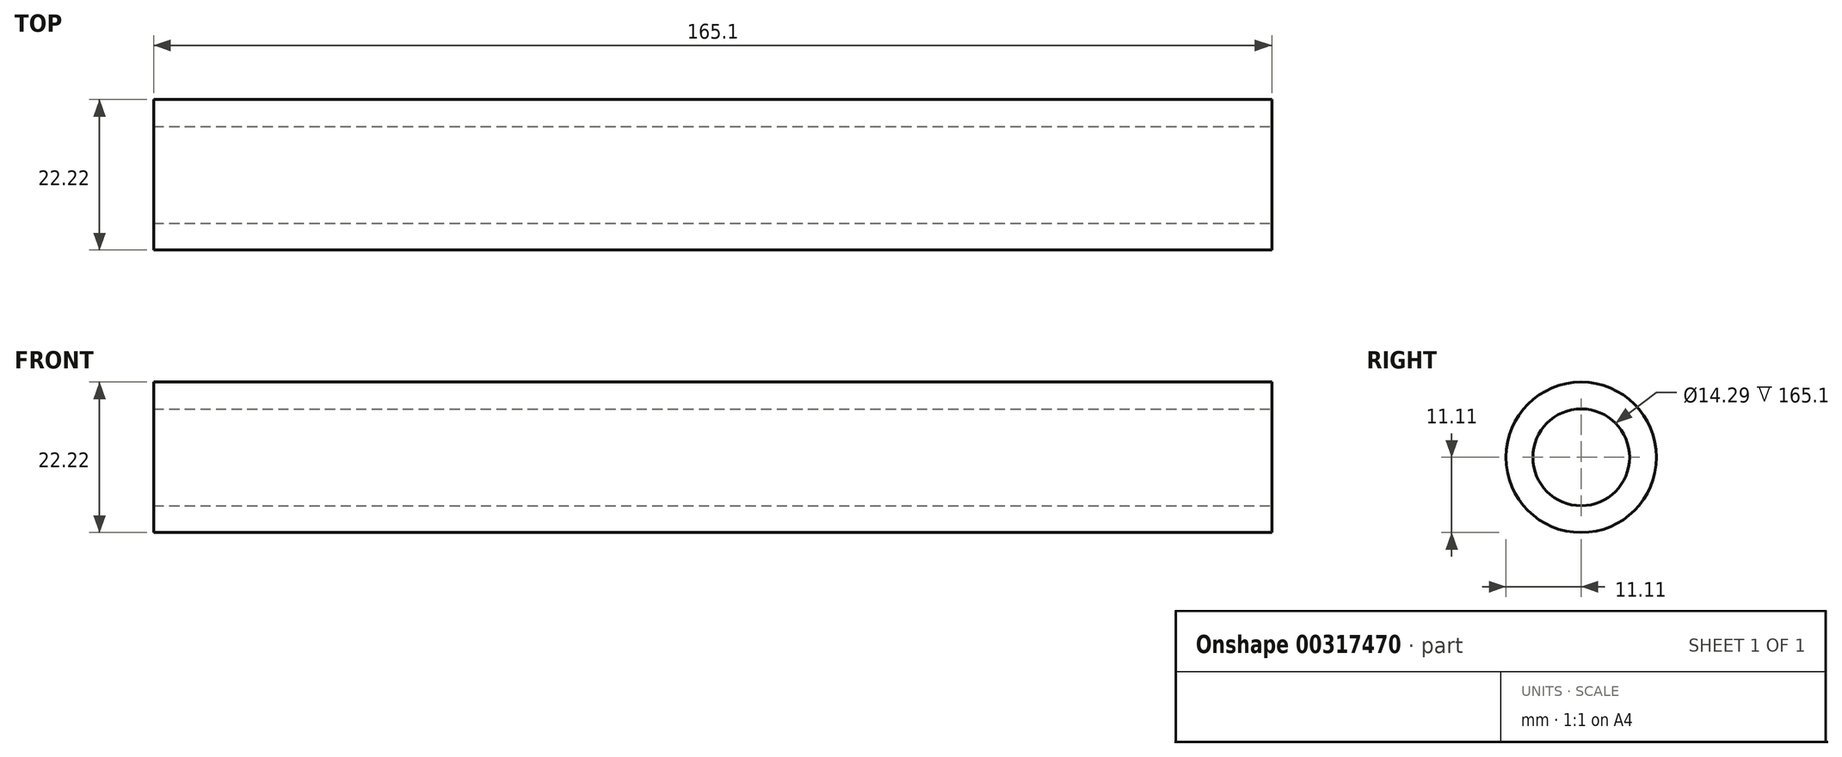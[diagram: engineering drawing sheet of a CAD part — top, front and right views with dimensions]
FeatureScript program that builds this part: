
annotation { "Feature Type Name" : "Feature", "Feature Type Description" : "" }
export const myFeature = defineFeature(function(context is Context, id is Id, definition is map)
    precondition{}
    {
        {
            var Q0;
            Q0=qCreatedBy(makeId("Right.planeOp"),FACE);
            var sketch = newSketch(context, id + "F0", { "sketchPlane" : qUnion([Q0])});
            skCircle(sketch, "E0", {"center": v(0, 0) * mm, "radius": 11.11 * mm});
            skSolve(sketch);
        }
        {
            var Q0;
            Q0=makeQuery(id+"F0.imprint","IMPRINT",FACE,{"disambiguationData":[TD([[makeQuery(id+"F0.imprint","IMPRINT",EDGE,{"derivedFrom":sQuery(id+"F0.wireOp",EDGE,"E0")}),1.0]])]});
            extrude(context, id + "F1", {"entities" : qUnion([Q0]), "endBound" : BoundingType.SYMMETRIC, "depth" : 165.1 * mm});
        }
        {
            var Q0;
            Q0=makeQuery(id+"F1.opExtrude","CAP_FACE",FACE,{"disambiguationData":[OSD([sQuery(id+"F0.wireOp",EDGE,"E0")])],"isStart":false});
            var sketch = newSketch(context, id + "F2", { "sketchPlane" : qUnion([Q0])});
            skCircle(sketch, "E1", {"center": v(0, 0) * mm, "radius": 7.14 * mm});
            skSolve(sketch);
        }
        {
            var Q0;
            Q0=makeQuery(id+"F2.imprint","IMPRINT",FACE,{"disambiguationData":[TD([[makeQuery(id+"F2.imprint","IMPRINT",EDGE,{"derivedFrom":sQuery(id+"F2.wireOp",EDGE,"E1")}),1.0]])]});
            extrude(context, id + "F3", {"entities" : qUnion([Q0]), "operationType" : NewBodyOperationType.REMOVE, "oppositeDirection" : true, "depth" : 165.1 * mm});
        }
    });
